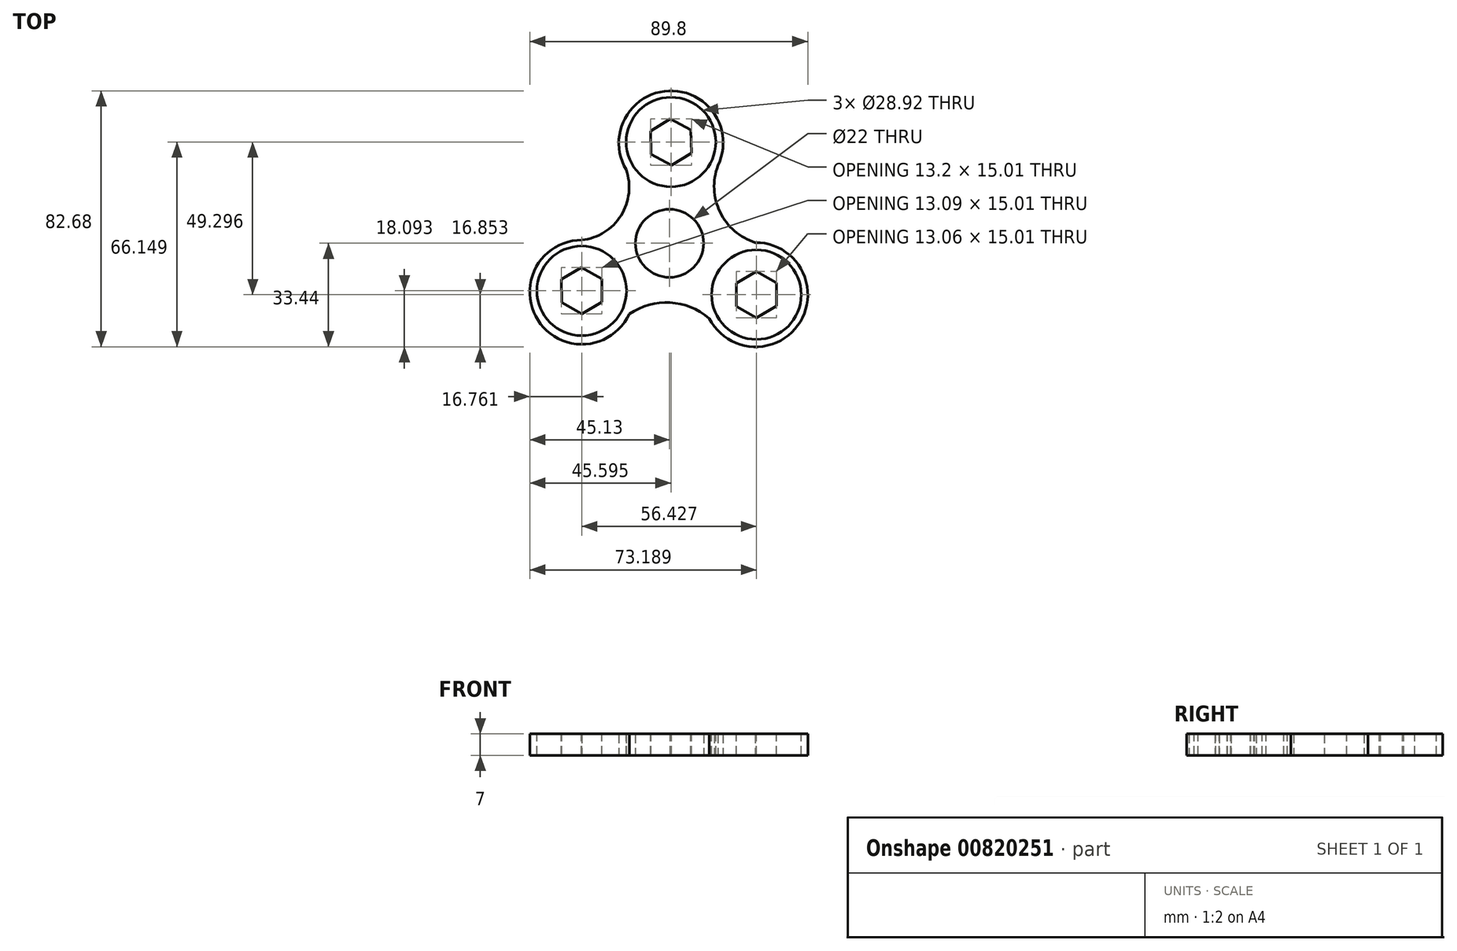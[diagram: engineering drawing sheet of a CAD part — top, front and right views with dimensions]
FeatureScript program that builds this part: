
annotation { "Feature Type Name" : "Feature", "Feature Type Description" : "" }
export const myFeature = defineFeature(function(context is Context, id is Id, definition is map)
    precondition{}
    {
        {
            var Q0;
            Q0=qCreatedBy(makeId("Top.planeOp"),FACE);
            var sketch = newSketch(context, id + "F0", { "sketchPlane" : qUnion([Q0])});
            skCircle(sketch, "E0", {"center": v(0, 0) * mm, "radius": 16.84 * mm});
            skCircle(sketch, "E1", {"center": v(0, 0) * mm, "radius": 11 * mm});
            skCircle(sketch, "E2", {"center": v(0.47, 32.4) * mm, "radius": 16.84 * mm});
            skCircle(sketch, "E3", {"center": v(0.47, 32.7) * mm, "radius": 14.46 * mm});
            skCircle(sketch, "E4.1.0", {"center": v(-28.3, -15.8) * mm, "radius": 16.84 * mm});
            skCircle(sketch, "E4.2.0", {"center": v(27.83, -16.6) * mm, "radius": 16.84 * mm});
            skCircle(sketch, "E5", {"center": v(-28.37, -15.35) * mm, "radius": 14.46 * mm});
            skCircle(sketch, "E6", {"center": v(28.06, -16.59) * mm, "radius": 14.46 * mm});
            skLineSegment(sketch, "E7", {"start": v(0.47, 32.7) * mm, "end": v(28.06, -16.59) * mm, "construction": true});
            skArc(sketch, "E8", {"start": v(12.83, -24.27) * mm, "mid": v(0.15, -19.16) * mm, "end": v(-13, -22.87) * mm});
            skArc(sketch, "E9", {"start": v(-28.3, 1.05) * mm, "mid": v(-15.67, 8.98) * mm, "end": v(-14.01, 23.8) * mm});
            skArc(sketch, "E10", {"start": v(15.62, 25.05) * mm, "mid": v(16.32, 10.05) * mm, "end": v(27.68, 0.24) * mm});
            skSolve(sketch);
        }
        {
            var Q0;
            {var subQ5=sQuery(id+"F0.wireOp",EDGE,"E9");Q0=makeQuery(id+"F0.imprint","IMPRINT",FACE,{"disambiguationData":[TD([[makeQuery(id+"F0.imprint","IMPRINT",EDGE,{"derivedFrom":subQ5}),-1.0]])]});}
            var Q1;
            {var subQ5=sQuery(id+"F0.wireOp",EDGE,"E10");Q1=makeQuery(id+"F0.imprint","IMPRINT",FACE,{"disambiguationData":[TD([[makeQuery(id+"F0.imprint","IMPRINT",EDGE,{"derivedFrom":subQ5}),-1.0]])]});}
            var Q2;
            {var subQ0=sQuery(id+"F0.wireOp",EDGE,"E2");var subQ1=sQuery(id+"F0.wireOp",EDGE,"E0");var subQ2=makeQuery(id+"F0.imprint","INTERSECT",VERTEX,{"disambiguationData":[OD(0.0)],"derivedFrom":[subQ1,subQ0]});Q2=makeQuery(id+"F0.imprint","IMPRINT",FACE,{"disambiguationData":[TD([[makeQuery(id+"F0.imprint","IMPRINT",EDGE,{"disambiguationData":[TD([[subQ2,1.0]])],"derivedFrom":subQ1}),1.0]])]});}
            var Q3;
            Q3=makeQuery(id+"F0.imprint","IMPRINT",FACE,{"disambiguationData":[TD([[makeQuery(id+"F0.imprint","IMPRINT",EDGE,{"derivedFrom":sQuery(id+"F0.wireOp",EDGE,"E1")}),-1.0]])]});
            var Q4;
            {var subQ0=sQuery(id+"F0.wireOp",EDGE,"E4.2.0");var subQ1=sQuery(id+"F0.wireOp",EDGE,"E0");var subQ2=makeQuery(id+"F0.imprint","INTERSECT",VERTEX,{"disambiguationData":[OD(0.0)],"derivedFrom":[subQ1,subQ0]});Q4=makeQuery(id+"F0.imprint","IMPRINT",FACE,{"disambiguationData":[TD([[makeQuery(id+"F0.imprint","IMPRINT",EDGE,{"disambiguationData":[TD([[subQ2,-1.0]])],"derivedFrom":subQ1}),1.0]])]});}
            var Q5;
            Q5=makeQuery(id+"F0.imprint","IMPRINT",FACE,{"disambiguationData":[TD([[makeQuery(id+"F0.imprint","IMPRINT",EDGE,{"derivedFrom":sQuery(id+"F0.wireOp",EDGE,"E6")}),-1.0]])]});
            var Q6;
            Q6=makeQuery(id+"F0.imprint","IMPRINT",FACE,{"disambiguationData":[TD([[makeQuery(id+"F0.imprint","IMPRINT",EDGE,{"derivedFrom":sQuery(id+"F0.wireOp",EDGE,"E3")}),-1.0]])]});
            var Q7;
            Q7=makeQuery(id+"F0.imprint","IMPRINT",FACE,{"disambiguationData":[TD([[makeQuery(id+"F0.imprint","IMPRINT",EDGE,{"derivedFrom":sQuery(id+"F0.wireOp",EDGE,"E5")}),-1.0]])]});
            var Q8;
            {var subQ0=sQuery(id+"F0.wireOp",EDGE,"E4.1.0");var subQ1=sQuery(id+"F0.wireOp",EDGE,"E0");var subQ2=makeQuery(id+"F0.imprint","INTERSECT",VERTEX,{"disambiguationData":[OD(0.0)],"derivedFrom":[subQ1,subQ0]});Q8=makeQuery(id+"F0.imprint","IMPRINT",FACE,{"disambiguationData":[TD([[makeQuery(id+"F0.imprint","IMPRINT",EDGE,{"disambiguationData":[TD([[subQ2,-1.0]])],"derivedFrom":subQ1}),1.0]])]});}
            var Q9;
            {var subQ5=sQuery(id+"F0.wireOp",EDGE,"E8");Q9=makeQuery(id+"F0.imprint","IMPRINT",FACE,{"disambiguationData":[TD([[makeQuery(id+"F0.imprint","IMPRINT",EDGE,{"derivedFrom":subQ5}),-1.0]])]});}
            extrude(context, id + "F1", {"entities" : qUnion([Q0, Q1, Q2, Q3, Q4, Q5, Q6, Q7, Q8, Q9]), "depth" : 7 * mm, "offsetDistance" : 25 * mm});
        }
        {
            var Q0;
            Q0=makeQuery(id+"F1.opExtrude","CAP_FACE",FACE,{"disambiguationData":[OSD([sQuery(id+"F0.wireOp",EDGE,"E1"),sQuery(id+"F0.wireOp",EDGE,"E2"),sQuery(id+"F0.wireOp",EDGE,"E3"),sQuery(id+"F0.wireOp",EDGE,"E4.1.0"),sQuery(id+"F0.wireOp",EDGE,"E4.2.0"),sQuery(id+"F0.wireOp",EDGE,"E5"),sQuery(id+"F0.wireOp",EDGE,"E6"),sQuery(id+"F0.wireOp",EDGE,"E8"),sQuery(id+"F0.wireOp",EDGE,"E9"),sQuery(id+"F0.wireOp",EDGE,"E10")])],"isStart":false});
            var sketch = newSketch(context, id + "F2", { "sketchPlane" : qUnion([Q0])});
            skCircle(sketch, "E11", {"center": v(0.47, 32.7) * mm, "radius": 8.04 * mm});
            skCircle(sketch, "E12.cCircle", {"center": v(0.47, 32.7) * mm, "radius": 6.5 * mm, "construction": true});
            skLineSegment(sketch, "E12.0", {"start": v(7.06, 29.13) * mm, "end": v(0.67, 25.2) * mm});
            skLineSegment(sketch, "E12.1", {"start": v(0.67, 25.2) * mm, "end": v(-5.93, 28.78) * mm});
            skLineSegment(sketch, "E12.2", {"start": v(-5.93, 28.78) * mm, "end": v(-6.13, 36.28) * mm});
            skLineSegment(sketch, "E12.3", {"start": v(-6.13, 36.28) * mm, "end": v(0.26, 40.21) * mm});
            skLineSegment(sketch, "E12.4", {"start": v(0.26, 40.21) * mm, "end": v(6.86, 36.64) * mm});
            skLineSegment(sketch, "E12.5", {"start": v(6.86, 36.64) * mm, "end": v(7.06, 29.13) * mm});
            skPoint(sketch, "E12.0.midPoint", {"position": v(3.87, 27.17) * mm});
            skCircle(sketch, "E13", {"center": v(28.06, -16.59) * mm, "radius": 8.56 * mm});
            skCircle(sketch, "E14.cCircle", {"center": v(28.06, -16.59) * mm, "radius": 6.5 * mm, "construction": true});
            skLineSegment(sketch, "E14.0", {"start": v(28, -9.08) * mm, "end": v(34.53, -12.78) * mm});
            skLineSegment(sketch, "E14.1", {"start": v(34.53, -12.78) * mm, "end": v(34.59, -20.29) * mm});
            skLineSegment(sketch, "E14.2", {"start": v(34.59, -20.29) * mm, "end": v(28.12, -24.1) * mm});
            skLineSegment(sketch, "E14.3", {"start": v(28.12, -24.1) * mm, "end": v(21.59, -20.4) * mm});
            skLineSegment(sketch, "E14.4", {"start": v(21.59, -20.4) * mm, "end": v(21.53, -12.89) * mm});
            skLineSegment(sketch, "E14.5", {"start": v(21.53, -12.89) * mm, "end": v(28, -9.08) * mm});
            skPoint(sketch, "E14.0.midPoint", {"position": v(31.26, -10.93) * mm});
            skCircle(sketch, "E15", {"center": v(-28.37, -15.35) * mm, "radius": 8.84 * mm});
            skCircle(sketch, "E16.cCircle", {"center": v(-28.37, -15.35) * mm, "radius": 6.5 * mm, "construction": true});
            skLineSegment(sketch, "E16.0", {"start": v(-28.46, -7.84) * mm, "end": v(-21.92, -11.51) * mm});
            skLineSegment(sketch, "E16.1", {"start": v(-21.92, -11.51) * mm, "end": v(-21.82, -19.02) * mm});
            skLineSegment(sketch, "E16.2", {"start": v(-21.82, -19.02) * mm, "end": v(-28.27, -22.85) * mm});
            skLineSegment(sketch, "E16.3", {"start": v(-28.27, -22.85) * mm, "end": v(-34.82, -19.18) * mm});
            skLineSegment(sketch, "E16.4", {"start": v(-34.82, -19.18) * mm, "end": v(-34.92, -11.68) * mm});
            skLineSegment(sketch, "E16.5", {"start": v(-34.92, -11.68) * mm, "end": v(-28.46, -7.84) * mm});
            skPoint(sketch, "E16.0.midPoint", {"position": v(-25.19, -9.68) * mm});
            skSolve(sketch);
        }
        {
            var Q0;
            Q0=makeQuery(id+"F2.imprint","IMPRINT",FACE,{"disambiguationData":[TD([[makeQuery(id+"F2.imprint","IMPRINT",EDGE,{"derivedFrom":sQuery(id+"F2.wireOp",EDGE,"E11")}),-1.0]])]});
            var Q1;
            Q1=makeQuery(id+"F2.imprint","IMPRINT",FACE,{"disambiguationData":[TD([[makeQuery(id+"F2.imprint","IMPRINT",EDGE,{"derivedFrom":sQuery(id+"F2.wireOp",EDGE,"E11")}),1.0]])]});
            var Q2;
            Q2=makeQuery(id+"F2.imprint","IMPRINT",FACE,{"disambiguationData":[TD([[makeQuery(id+"F2.imprint","IMPRINT",EDGE,{"derivedFrom":sQuery(id+"F2.wireOp",EDGE,"E15")}),-1.0]])]});
            var Q3;
            Q3=makeQuery(id+"F2.imprint","IMPRINT",FACE,{"disambiguationData":[TD([[makeQuery(id+"F2.imprint","IMPRINT",EDGE,{"derivedFrom":sQuery(id+"F2.wireOp",EDGE,"E15")}),1.0]])]});
            var Q4;
            Q4=makeQuery(id+"F2.imprint","IMPRINT",FACE,{"disambiguationData":[TD([[makeQuery(id+"F2.imprint","IMPRINT",EDGE,{"derivedFrom":sQuery(id+"F2.wireOp",EDGE,"E13")}),-1.0]])]});
            var Q5;
            Q5=makeQuery(id+"F2.imprint","IMPRINT",FACE,{"disambiguationData":[TD([[makeQuery(id+"F2.imprint","IMPRINT",EDGE,{"derivedFrom":sQuery(id+"F2.wireOp",EDGE,"E13")}),1.0]])]});
            extrude(context, id + "F3", {"entities" : qUnion([Q0, Q1, Q2, Q3, Q4, Q5]), "oppositeDirection" : true, "depth" : 7 * mm, "offsetDistance" : 25 * mm});
        }
    });
